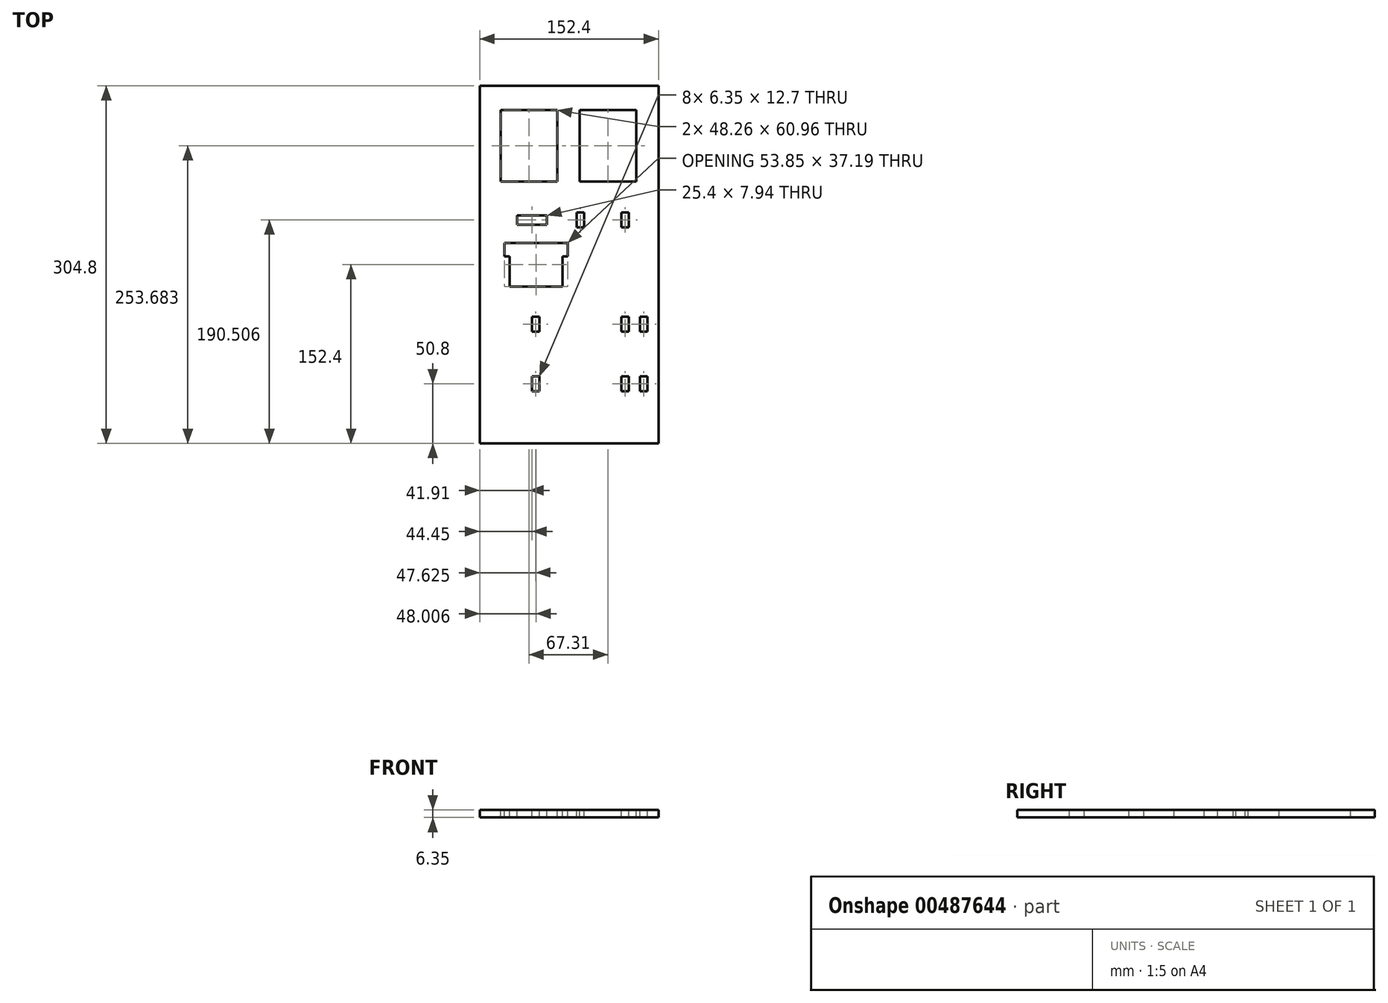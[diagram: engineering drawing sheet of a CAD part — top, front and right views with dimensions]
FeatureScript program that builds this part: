
annotation { "Feature Type Name" : "Feature", "Feature Type Description" : "" }
export const myFeature = defineFeature(function(context is Context, id is Id, definition is map)
    precondition{}
    {
        {
            var Q0;
            Q0=qCreatedBy(makeId("Top.planeOp"),FACE);
            var sketch = newSketch(context, id + "F0", { "sketchPlane" : qUnion([Q0])});
            skLineSegment(sketch, "E0.bottom", {"start": v(0, 0) * mm, "end": v(152.4, 0) * mm});
            skLineSegment(sketch, "E0.top", {"start": v(0, 304.8) * mm, "end": v(152.4, 304.8) * mm});
            skLineSegment(sketch, "E0.left", {"start": v(0, 0) * mm, "end": v(0, 304.8) * mm});
            skLineSegment(sketch, "E0.right", {"start": v(152.4, 0) * mm, "end": v(152.4, 304.8) * mm});
            skSolve(sketch);
        }
        {
            var Q0;
            Q0 = qSketchRegion(id + "F0", true);
            extrude(context, id + "F1", {"entities" : qUnion([Q0]), "depth" : 6.35 * mm});
        }
        {
            var Q0;
            Q0=makeQuery(id+"F1.opExtrude","CAP_FACE",FACE,{"disambiguationData":[OSD([sQuery(id+"F0.wireOp",EDGE,"E0.bottom"),sQuery(id+"F0.wireOp",EDGE,"E0.top"),sQuery(id+"F0.wireOp",EDGE,"E0.left"),sQuery(id+"F0.wireOp",EDGE,"E0.right")])],"isStart":false});
            var sketch = newSketch(context, id + "F2", { "sketchPlane" : qUnion([Q0])});
            skLineSegment(sketch, "E1", {"start": v(0, 50.8) * mm, "end": v(152.4, 50.8) * mm, "construction": true});
            skLineSegment(sketch, "E2", {"start": v(0, 190.5) * mm, "end": v(152.4, 190.5) * mm, "construction": true});
            skLineSegment(sketch, "E3", {"start": v(0, 101.6) * mm, "end": v(148, 101.6) * mm, "construction": true});
            skLineSegment(sketch, "E4", {"start": v(0, 254) * mm, "end": v(152.4, 254) * mm, "construction": true});
            skLineSegment(sketch, "E5.bottom", {"start": v(120.65, 57.15) * mm, "end": v(127, 57.15) * mm});
            skLineSegment(sketch, "E5.top", {"start": v(120.65, 44.45) * mm, "end": v(127, 44.45) * mm});
            skLineSegment(sketch, "E5.left", {"start": v(120.65, 57.15) * mm, "end": v(120.65, 44.45) * mm});
            skLineSegment(sketch, "E5.right", {"start": v(127, 57.15) * mm, "end": v(127, 44.45) * mm});
            skLineSegment(sketch, "E6.1.0.0", {"start": v(44.45, 44.45) * mm, "end": v(50.8, 44.45) * mm});
            skLineSegment(sketch, "E6.1.0.1", {"start": v(44.45, 57.15) * mm, "end": v(44.45, 44.45) * mm});
            skLineSegment(sketch, "E6.1.0.2", {"start": v(44.45, 57.15) * mm, "end": v(50.8, 57.15) * mm});
            skLineSegment(sketch, "E6.1.0.3", {"start": v(50.8, 57.15) * mm, "end": v(50.8, 44.45) * mm});
            skLineSegment(sketch, "E6.direction1", {"start": v(120.65, 44.45) * mm, "end": v(44.45, 44.45) * mm, "construction": true});
            skLineSegment(sketch, "E7.0.1.0", {"start": v(127, 107.95) * mm, "end": v(127, 95.25) * mm});
            skLineSegment(sketch, "E7.0.1.1", {"start": v(44.45, 107.95) * mm, "end": v(44.45, 95.25) * mm});
            skLineSegment(sketch, "E7.0.1.2", {"start": v(120.65, 95.25) * mm, "end": v(44.45, 95.25) * mm, "construction": true});
            skLineSegment(sketch, "E7.0.1.3", {"start": v(50.8, 107.95) * mm, "end": v(50.8, 95.25) * mm});
            skLineSegment(sketch, "E7.0.1.4", {"start": v(120.65, 107.95) * mm, "end": v(120.65, 95.25) * mm});
            skLineSegment(sketch, "E7.0.1.5", {"start": v(44.45, 95.25) * mm, "end": v(50.8, 95.25) * mm});
            skLineSegment(sketch, "E7.0.1.6", {"start": v(120.65, 107.95) * mm, "end": v(127, 107.95) * mm});
            skLineSegment(sketch, "E7.0.1.7", {"start": v(120.65, 95.25) * mm, "end": v(127, 95.25) * mm});
            skLineSegment(sketch, "E7.0.1.8", {"start": v(44.45, 107.95) * mm, "end": v(50.8, 107.95) * mm});
            skLineSegment(sketch, "E7.direction1", {"start": v(44.45, 44.45) * mm, "end": v(69.85, 44.45) * mm, "construction": true});
            skLineSegment(sketch, "E7.direction2", {"start": v(44.45, 44.45) * mm, "end": v(44.45, 95.25) * mm, "construction": true});
            skLineSegment(sketch, "E8.bottom", {"start": v(120.65, 196.85) * mm, "end": v(127, 196.85) * mm});
            skLineSegment(sketch, "E8.top", {"start": v(120.65, 184.15) * mm, "end": v(127, 184.15) * mm});
            skLineSegment(sketch, "E8.left", {"start": v(120.65, 196.85) * mm, "end": v(120.65, 184.15) * mm});
            skLineSegment(sketch, "E8.right", {"start": v(127, 196.85) * mm, "end": v(127, 184.15) * mm});
            skLineSegment(sketch, "E9.1.0.0", {"start": v(88.9, 196.85) * mm, "end": v(88.9, 184.15) * mm});
            skLineSegment(sketch, "E9.1.0.1", {"start": v(82.55, 196.85) * mm, "end": v(88.9, 196.85) * mm});
            skLineSegment(sketch, "E9.1.0.2", {"start": v(82.55, 196.85) * mm, "end": v(82.55, 184.15) * mm});
            skLineSegment(sketch, "E9.1.0.3", {"start": v(82.55, 184.15) * mm, "end": v(88.9, 184.15) * mm});
            skLineSegment(sketch, "E9.direction1", {"start": v(120.65, 184.15) * mm, "end": v(82.55, 184.15) * mm, "construction": true});
            skLineSegment(sketch, "E10.bottom", {"start": v(85.09, 284.16) * mm, "end": v(133.35, 284.16) * mm});
            skLineSegment(sketch, "E10.top", {"start": v(85.09, 223.2) * mm, "end": v(133.35, 223.2) * mm});
            skLineSegment(sketch, "E10.left", {"start": v(85.09, 284.16) * mm, "end": v(85.09, 223.2) * mm});
            skLineSegment(sketch, "E10.right", {"start": v(133.35, 284.16) * mm, "end": v(133.35, 223.2) * mm});
            skLineSegment(sketch, "E11.bottom", {"start": v(31.75, 194.48) * mm, "end": v(57.15, 194.48) * mm});
            skLineSegment(sketch, "E11.top", {"start": v(31.75, 186.54) * mm, "end": v(57.15, 186.54) * mm});
            skLineSegment(sketch, "E11.left", {"start": v(31.75, 194.48) * mm, "end": v(31.75, 186.54) * mm});
            skLineSegment(sketch, "E11.right", {"start": v(57.15, 194.48) * mm, "end": v(57.15, 186.54) * mm});
            skLineSegment(sketch, "E12.top", {"start": v(25.4, 133.8) * mm, "end": v(70.61, 133.8) * mm});
            skLineSegment(sketch, "E12.left", {"start": v(25.4, 159.56) * mm, "end": v(25.4, 133.8) * mm});
            skLineSegment(sketch, "E12.right", {"start": v(70.61, 159.56) * mm, "end": v(70.61, 133.8) * mm});
            skLineSegment(sketch, "E13", {"start": v(0, 152.4) * mm, "end": v(152.4, 152.4) * mm, "construction": true});
            skLineSegment(sketch, "E14.top", {"start": v(25.4, 159.56) * mm, "end": v(21.08, 159.56) * mm});
            skLineSegment(sketch, "E14.right", {"start": v(21.08, 171) * mm, "end": v(21.08, 159.56) * mm});
            skLineSegment(sketch, "E15.top", {"start": v(70.61, 159.56) * mm, "end": v(74.93, 159.56) * mm});
            skLineSegment(sketch, "E15.right", {"start": v(74.93, 171) * mm, "end": v(74.93, 159.56) * mm});
            skLineSegment(sketch, "E16", {"start": v(75.56, 211.1) * mm, "end": v(75.56, 294.49) * mm, "construction": true});
            skLineSegment(sketch, "E17.MirrorCS", {"start": v(17.78, 284.16) * mm, "end": v(17.78, 223.2) * mm});
            skLineSegment(sketch, "E18.MirrorCS", {"start": v(66.04, 284.16) * mm, "end": v(17.78, 284.16) * mm});
            skLineSegment(sketch, "E19.MirrorCS", {"start": v(66.04, 284.16) * mm, "end": v(66.04, 223.2) * mm});
            skLineSegment(sketch, "E20.MirrorCS", {"start": v(66.04, 223.2) * mm, "end": v(17.78, 223.2) * mm});
            skLineSegment(sketch, "E21", {"start": v(74.93, 171) * mm, "end": v(21.08, 171) * mm});
            skSolve(sketch);
        }
        {
            var Q0;
            Q0 = qSketchRegion(id + "F2", true);
            extrude(context, id + "F3", {"entities" : qUnion([Q0]), "operationType" : NewBodyOperationType.REMOVE, "endBound" : BoundingType.THROUGH_ALL, "oppositeDirection" : true, "depth" : 25.4 * mm});
        }
        {
            var Q0;
            Q0=makeQuery(id+"F1.opExtrude","CAP_FACE",FACE,{"disambiguationData":[OSD([sQuery(id+"F0.wireOp",EDGE,"E0.bottom"),sQuery(id+"F0.wireOp",EDGE,"E0.top"),sQuery(id+"F0.wireOp",EDGE,"E0.left"),sQuery(id+"F0.wireOp",EDGE,"E0.right")])],"isStart":false});
            var sketch = newSketch(context, id + "F4", { "sketchPlane" : qUnion([Q0])});
            skLineSegment(sketch, "E22.bottom", {"start": v(136.75, 44.45) * mm, "end": v(143.1, 44.45) * mm});
            skLineSegment(sketch, "E22.top", {"start": v(136.75, 57.15) * mm, "end": v(143.1, 57.15) * mm});
            skLineSegment(sketch, "E22.left", {"start": v(136.75, 44.45) * mm, "end": v(136.75, 57.15) * mm});
            skLineSegment(sketch, "E22.right", {"start": v(143.1, 44.45) * mm, "end": v(143.1, 57.15) * mm});
            skLineSegment(sketch, "E23", {"start": v(123.82, 44.45) * mm, "end": v(156.3, 44.45) * mm, "construction": true});
            skLineSegment(sketch, "E24.0.1.0", {"start": v(136.75, 95.25) * mm, "end": v(143.1, 95.25) * mm});
            skLineSegment(sketch, "E24.0.1.1", {"start": v(136.75, 107.95) * mm, "end": v(143.1, 107.95) * mm});
            skLineSegment(sketch, "E24.0.1.2", {"start": v(136.75, 95.25) * mm, "end": v(136.75, 107.95) * mm});
            skLineSegment(sketch, "E24.0.1.3", {"start": v(143.1, 95.25) * mm, "end": v(143.1, 107.95) * mm});
            skLineSegment(sketch, "E24.direction1", {"start": v(136.75, 44.45) * mm, "end": v(162.15, 44.45) * mm, "construction": true});
            skLineSegment(sketch, "E24.direction2", {"start": v(136.75, 44.45) * mm, "end": v(136.75, 95.25) * mm, "construction": true});
            skSolve(sketch);
        }
        {
            var Q0;
            Q0 = qSketchRegion(id + "F4", true);
            extrude(context, id + "F5", {"entities" : qUnion([Q0]), "operationType" : NewBodyOperationType.REMOVE, "oppositeDirection" : true, "depth" : 25.4 * mm});
        }
    });
